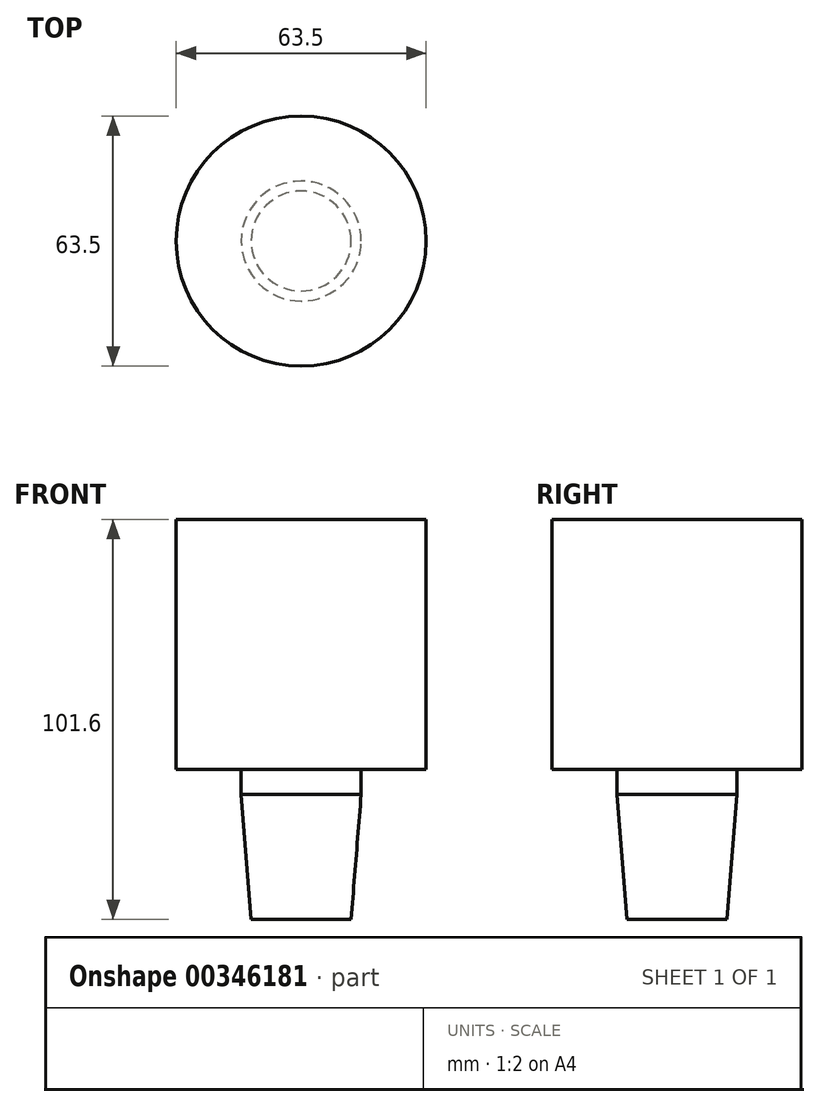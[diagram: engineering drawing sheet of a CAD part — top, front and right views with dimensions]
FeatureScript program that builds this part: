
annotation { "Feature Type Name" : "Feature", "Feature Type Description" : "" }
export const myFeature = defineFeature(function(context is Context, id is Id, definition is map)
    precondition{}
    {
        {
            var Q0;
            Q0=qCreatedBy(makeId("Front.planeOp"),FACE);
            var sketch = newSketch(context, id + "F0", { "sketchPlane" : qUnion([Q0])});
            skLineSegment(sketch, "E0", {"start": v(0, 0) * mm, "end": v(0, -101.6) * mm});
            skLineSegment(sketch, "E1", {"start": v(0, -101.6) * mm, "end": v(12.7, -101.6) * mm});
            skLineSegment(sketch, "E2", {"start": v(12.7, -101.6) * mm, "end": v(15.24, -69.85) * mm});
            skLineSegment(sketch, "E3", {"start": v(15.24, -69.85) * mm, "end": v(15.24, -63.5) * mm});
            skLineSegment(sketch, "E4", {"start": v(15.24, -63.5) * mm, "end": v(31.75, -63.5) * mm});
            skLineSegment(sketch, "E5", {"start": v(31.75, -63.5) * mm, "end": v(31.75, 0) * mm});
            skLineSegment(sketch, "E6", {"start": v(31.75, 0) * mm, "end": v(0, 0) * mm});
            skSolve(sketch);
        }
        {
            var Q0;
            Q0 = qSketchRegion(id + "F0", true);
            var Q1;
            Q1=sQuery(id+"F0.wireOp",EDGE,"E0");
            revolve(context, id + "F1", {"entities" : qUnion([Q0]), "axis" : qUnion([Q1]), "revolveType" : RevolveType.FULL});
        }
    });
